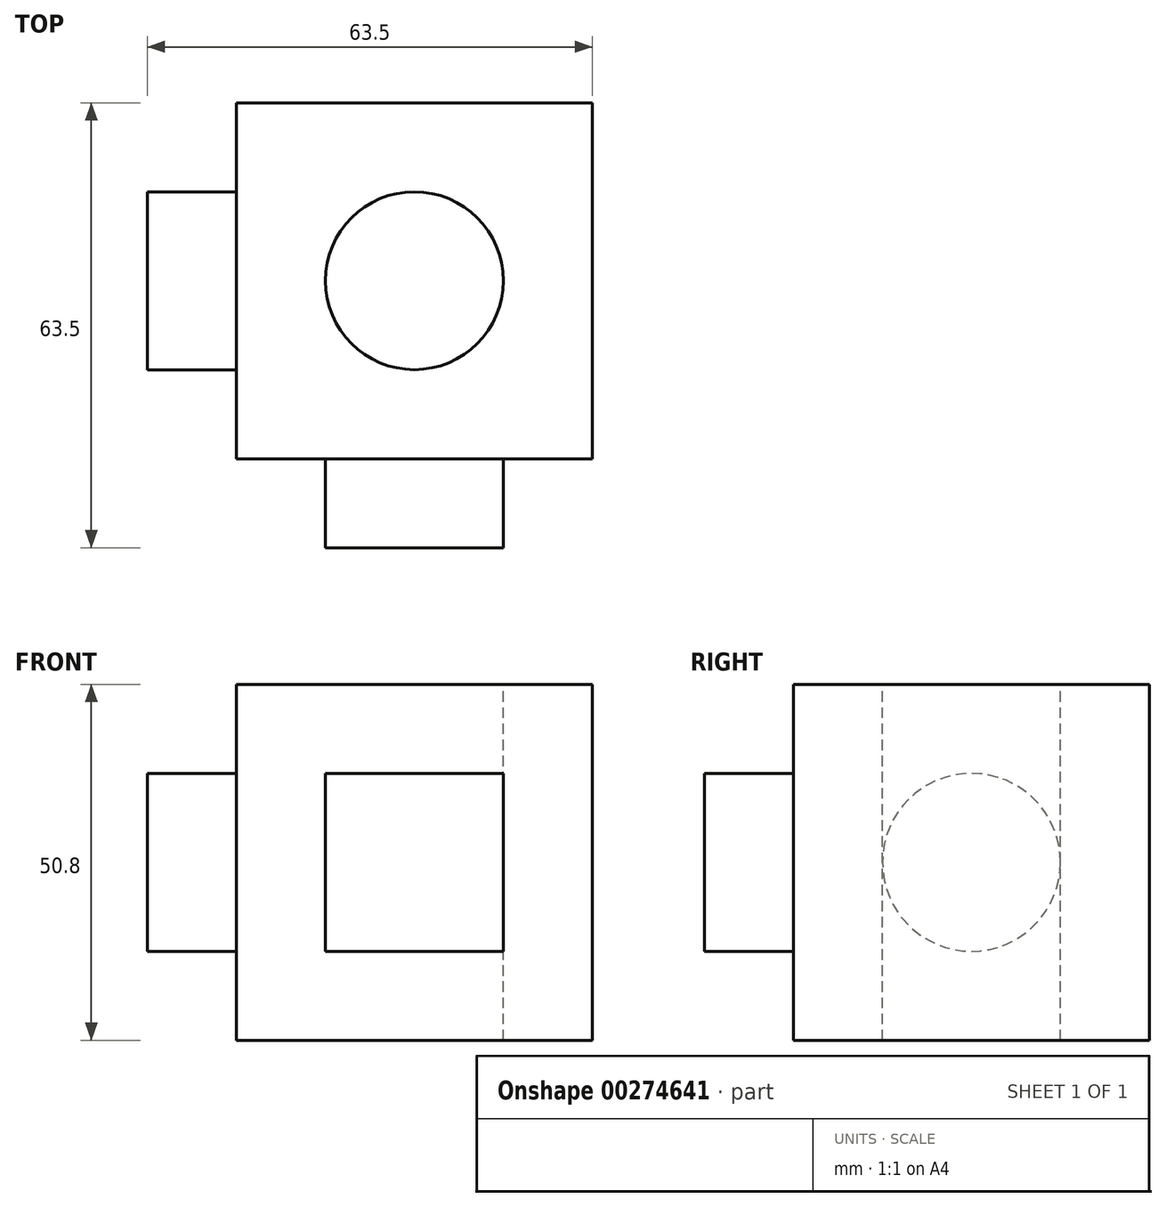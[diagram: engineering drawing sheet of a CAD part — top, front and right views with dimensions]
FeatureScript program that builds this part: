
annotation { "Feature Type Name" : "Feature", "Feature Type Description" : "" }
export const myFeature = defineFeature(function(context is Context, id is Id, definition is map)
    precondition{}
    {
        {
            var Q0;
            Q0=qCreatedBy(makeId("Front.planeOp"),FACE);
            var sketch = newSketch(context, id + "F0", { "sketchPlane" : qUnion([Q0])});
            skLineSegment(sketch, "E0.bottom", {"start": v(0, 0) * mm, "end": v(-50.8, 0) * mm});
            skLineSegment(sketch, "E0.top", {"start": v(0, 50.8) * mm, "end": v(-50.8, 50.8) * mm});
            skLineSegment(sketch, "E0.left", {"start": v(0, 0) * mm, "end": v(0, 50.8) * mm});
            skLineSegment(sketch, "E0.right", {"start": v(-50.8, 0) * mm, "end": v(-50.8, 50.8) * mm});
            skSolve(sketch);
        }
        {
            var Q0;
            Q0 = qSketchRegion(id + "F0", true);
            extrude(context, id + "F1", {"entities" : qUnion([Q0]), "depth" : 50.8 * mm});
        }
        {
            var Q0;
            Q0=makeQuery(id+"F1.opExtrude","CAP_FACE",FACE,{"disambiguationData":[OSD([sQuery(id+"F0.wireOp",EDGE,"E0.bottom"),sQuery(id+"F0.wireOp",EDGE,"E0.top"),sQuery(id+"F0.wireOp",EDGE,"E0.left"),sQuery(id+"F0.wireOp",EDGE,"E0.right")])],"isStart":false});
            var sketch = newSketch(context, id + "F2", { "sketchPlane" : qUnion([Q0])});
            skLineSegment(sketch, "E1.bottom", {"start": v(-12.7, 12.7) * mm, "end": v(-38.1, 12.7) * mm});
            skLineSegment(sketch, "E1.top", {"start": v(-12.7, 38.1) * mm, "end": v(-38.1, 38.1) * mm});
            skLineSegment(sketch, "E1.left", {"start": v(-12.7, 12.7) * mm, "end": v(-12.7, 38.1) * mm});
            skLineSegment(sketch, "E1.right", {"start": v(-38.1, 12.7) * mm, "end": v(-38.1, 38.1) * mm});
            skSolve(sketch);
        }
        {
            var Q0;
            Q0 = qSketchRegion(id + "F2", true);
            extrude(context, id + "F3", {"entities" : qUnion([Q0]), "operationType" : NewBodyOperationType.ADD, "depth" : 12.7 * mm});
        }
        {
            var Q0;
            Q0=makeQuery(id+"F1.opExtrude","SWEPT_FACE",FACE,{"disambiguationData":[OSD([sQuery(id+"F0.wireOp",EDGE,"E0.right")])]});
            var sketch = newSketch(context, id + "F4", { "sketchPlane" : qUnion([Q0])});
            skCircle(sketch, "E2", {"center": v(25.4, 25.4) * mm, "radius": 12.7 * mm});
            skSolve(sketch);
        }
        {
            var Q0;
            Q0 = qSketchRegion(id + "F4", true);
            extrude(context, id + "F5", {"entities" : qUnion([Q0]), "operationType" : NewBodyOperationType.ADD, "depth" : 12.7 * mm});
        }
        {
            var Q0;
            Q0=makeQuery(id+"F1.opExtrude","SWEPT_FACE",FACE,{"disambiguationData":[OSD([sQuery(id+"F0.wireOp",EDGE,"E0.top")])]});
            var sketch = newSketch(context, id + "F6", { "sketchPlane" : qUnion([Q0])});
            skCircle(sketch, "E3", {"center": v(-25.4, -25.4) * mm, "radius": 12.7 * mm});
            skSolve(sketch);
        }
        {
            var Q0;
            Q0 = qSketchRegion(id + "F6", true);
            extrude(context, id + "F7", {"entities" : qUnion([Q0]), "operationType" : NewBodyOperationType.REMOVE, "oppositeDirection" : true, "depth" : 50.8 * mm});
        }
    });
